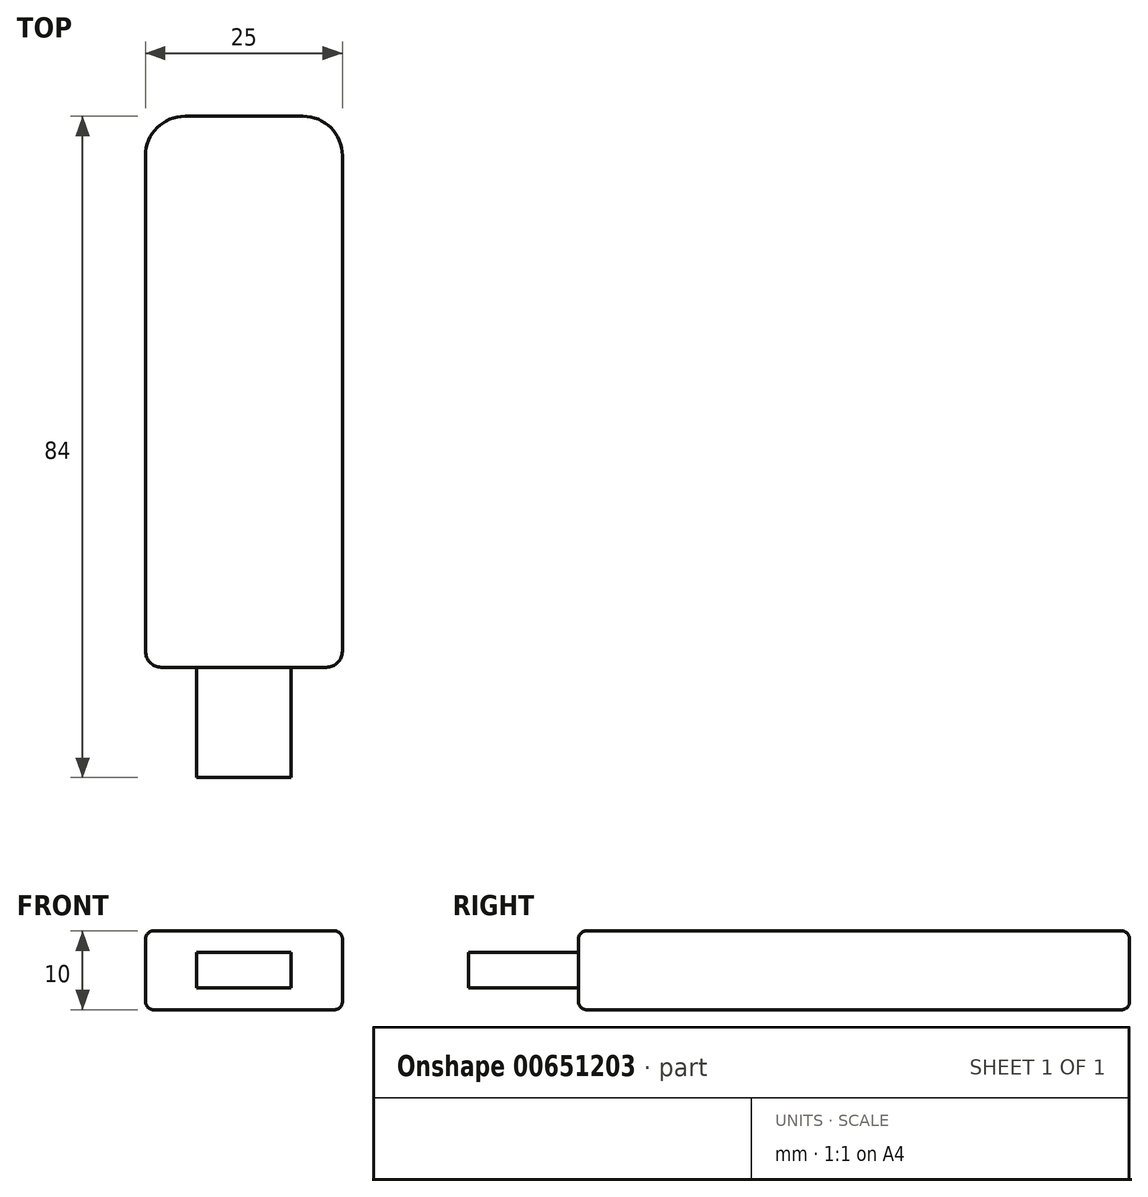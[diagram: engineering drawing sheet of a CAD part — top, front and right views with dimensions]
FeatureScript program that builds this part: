
annotation { "Feature Type Name" : "Feature", "Feature Type Description" : "" }
export const myFeature = defineFeature(function(context is Context, id is Id, definition is map)
    precondition{}
    {
        {
            var Q0;
            Q0=qCreatedBy(makeId("Top.planeOp"),FACE);
            var sketch = newSketch(context, id + "F0", { "sketchPlane" : qUnion([Q0])});
            skLineSegment(sketch, "E0.bottom", {"start": v(-12.5, 35) * mm, "end": v(12.5, 35) * mm});
            skLineSegment(sketch, "E0.top", {"start": v(-12.5, -35) * mm, "end": v(12.5, -35) * mm});
            skLineSegment(sketch, "E0.left", {"start": v(-12.5, 35) * mm, "end": v(-12.5, -35) * mm});
            skLineSegment(sketch, "E0.right", {"start": v(12.5, 35) * mm, "end": v(12.5, -35) * mm});
            skPoint(sketch, "E0.middle", {"position": v(0, 0) * mm});
            skSolve(sketch);
        }
        {
            var Q0;
            Q0=makeQuery(id+"F0.imprint","IMPRINT",FACE,{"disambiguationData":[TD([[makeQuery(id+"F0.imprint","IMPRINT",EDGE,{"derivedFrom":sQuery(id+"F0.wireOp",EDGE,"E0.bottom")}),-1.0]])]});
            extrude(context, id + "F1", {"entities" : qUnion([Q0]), "endBound" : BoundingType.SYMMETRIC, "depth" : 10 * mm, "offsetDistance" : 25 * mm});
        }
        {
            var Q0;
            Q0=makeQuery(id+"F1.opExtrude","SWEPT_FACE",FACE,{"disambiguationData":[OSD([sQuery(id+"F0.wireOp",EDGE,"E0.top")])]});
            var sketch = newSketch(context, id + "F2", { "sketchPlane" : qUnion([Q0])});
            skLineSegment(sketch, "E1.bottom", {"start": v(-6, 2.25) * mm, "end": v(6, 2.25) * mm});
            skLineSegment(sketch, "E1.top", {"start": v(-6, -2.25) * mm, "end": v(6, -2.25) * mm});
            skLineSegment(sketch, "E1.left", {"start": v(-6, 2.25) * mm, "end": v(-6, -2.25) * mm});
            skLineSegment(sketch, "E1.right", {"start": v(6, 2.25) * mm, "end": v(6, -2.25) * mm});
            skPoint(sketch, "E1.middle", {"position": v(0, 0) * mm});
            skSolve(sketch);
        }
        {
            var Q0;
            Q0=makeQuery(id+"F2.imprint","IMPRINT",FACE,{"disambiguationData":[TD([[makeQuery(id+"F2.imprint","IMPRINT",EDGE,{"derivedFrom":sQuery(id+"F2.wireOp",EDGE,"E1.bottom")}),-1.0]])]});
            extrude(context, id + "F3", {"entities" : qUnion([Q0]), "operationType" : NewBodyOperationType.ADD, "depth" : 14 * mm, "offsetDistance" : 25 * mm});
        }
        {
            var Q0;
            Q0=makeQuery(id+"F1.opExtrude","SWEPT_EDGE",EDGE,{"disambiguationData":[OSD([sQuery(id+"F0.wireOp",EDGE,"E0.top"),sQuery(id+"F0.wireOp",EDGE,"E0.right")])]});
            var Q1;
            Q1=makeQuery(id+"F1.opExtrude","SWEPT_EDGE",EDGE,{"disambiguationData":[OSD([sQuery(id+"F0.wireOp",EDGE,"E0.top"),sQuery(id+"F0.wireOp",EDGE,"E0.left")])]});
            fillet(context, id + "F4", {"entities" : qUnion([Q0, Q1]), "tangentPropagation" : true, "radius" : 2 * mm, "defaultsChanged" : true, "vertexSettings" : [], "allowEdgeOverflow" : false});
        }
        {
            var Q0;
            Q0=makeQuery(id+"F1.opExtrude","SWEPT_EDGE",EDGE,{"disambiguationData":[OSD([sQuery(id+"F0.wireOp",EDGE,"E0.bottom"),sQuery(id+"F0.wireOp",EDGE,"E0.right")])]});
            var Q1;
            Q1=makeQuery(id+"F1.opExtrude","SWEPT_EDGE",EDGE,{"disambiguationData":[OSD([sQuery(id+"F0.wireOp",EDGE,"E0.bottom"),sQuery(id+"F0.wireOp",EDGE,"E0.left")])]});
            fillet(context, id + "F5", {"entities" : qUnion([Q0, Q1]), "tangentPropagation" : true, "radius" : 5 * mm, "defaultsChanged" : false, "vertexSettings" : [], "allowEdgeOverflow" : false});
        }
        {
            var Q0;
            Q0=makeQuery(id+"F1.opExtrude","CAP_FACE",FACE,{"disambiguationData":[OSD([sQuery(id+"F0.wireOp",EDGE,"E0.bottom"),sQuery(id+"F0.wireOp",EDGE,"E0.top"),sQuery(id+"F0.wireOp",EDGE,"E0.left"),sQuery(id+"F0.wireOp",EDGE,"E0.right")])],"isStart":false});
            var Q1;
            Q1=makeQuery(id+"F1.opExtrude","CAP_FACE",FACE,{"disambiguationData":[OSD([sQuery(id+"F0.wireOp",EDGE,"E0.bottom"),sQuery(id+"F0.wireOp",EDGE,"E0.top"),sQuery(id+"F0.wireOp",EDGE,"E0.left"),sQuery(id+"F0.wireOp",EDGE,"E0.right")])],"isStart":true});
            fillet(context, id + "F6", {"entities" : qUnion([Q0, Q1]), "tangentPropagation" : true, "radius" : 1 * mm, "defaultsChanged" : true, "vertexSettings" : [], "allowEdgeOverflow" : false});
        }
    });
